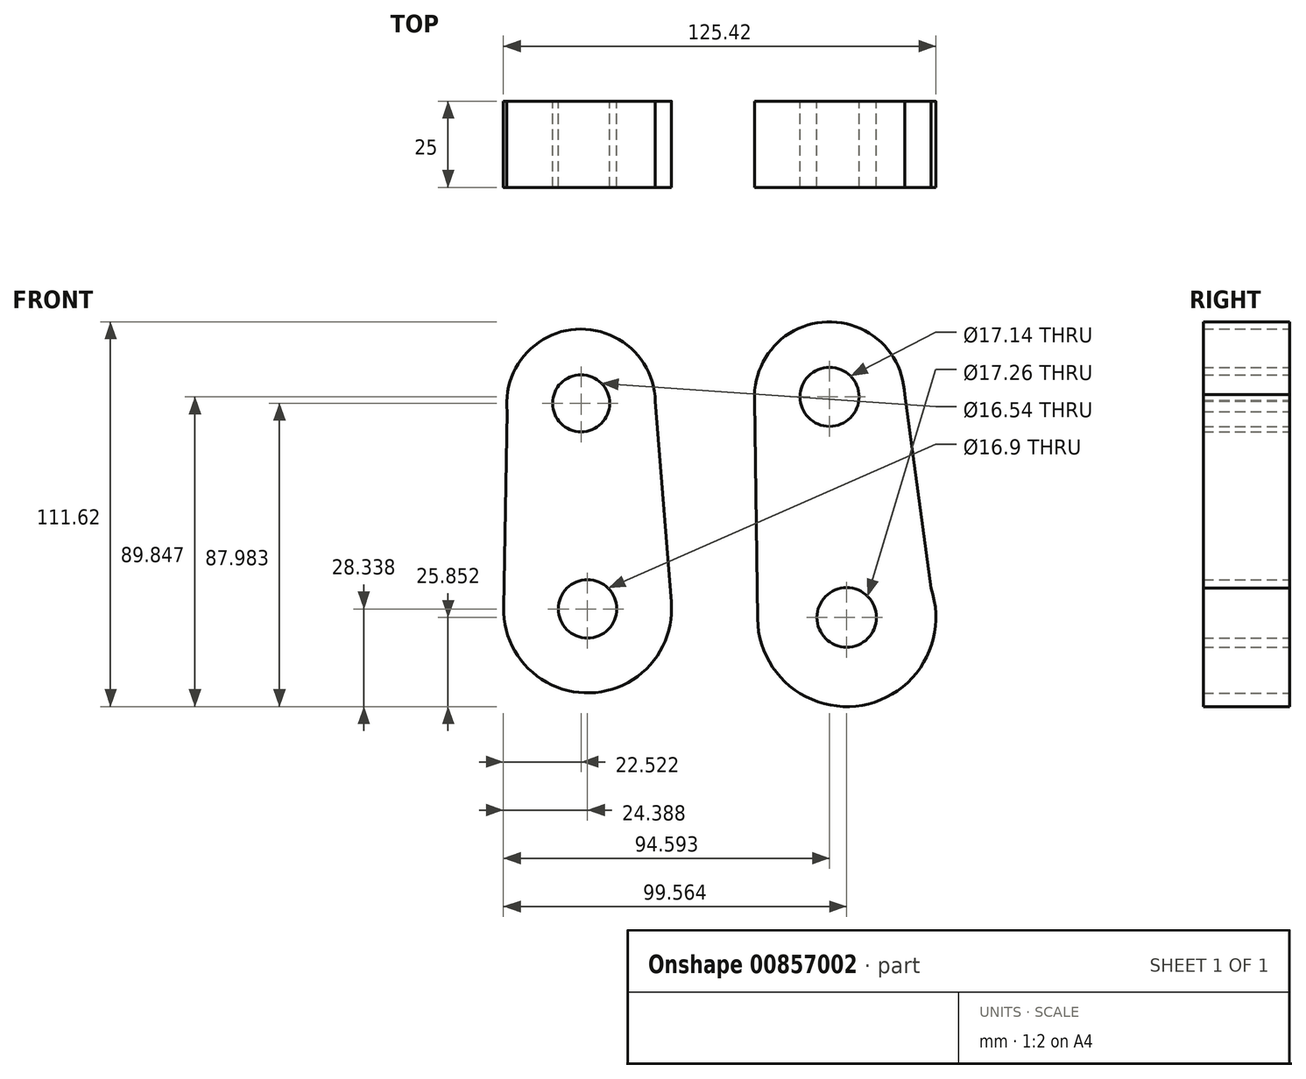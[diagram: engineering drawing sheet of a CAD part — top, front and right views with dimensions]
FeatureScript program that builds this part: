
annotation { "Feature Type Name" : "Feature", "Feature Type Description" : "" }
export const myFeature = defineFeature(function(context is Context, id is Id, definition is map)
    precondition{}
    {
        {
            var Q0;
            Q0=qCreatedBy(makeId("Front.planeOp"),FACE);
            var sketch = newSketch(context, id + "F0", { "sketchPlane" : qUnion([Q0])});
            skCircle(sketch, "E0", {"center": v(37.43, 27.03) * mm, "radius": 21.77 * mm});
            skCircle(sketch, "E1", {"center": v(-34.64, 25.16) * mm, "radius": 21.53 * mm});
            skCircle(sketch, "E2", {"center": v(-32.77, -34.48) * mm, "radius": 24.38 * mm});
            skCircle(sketch, "E3", {"center": v(42.4, -36.97) * mm, "radius": 25.86 * mm});
            skLineSegment(sketch, "E4", {"start": v(59.2, 27.63) * mm, "end": v(66.8, -28.43) * mm});
            skLineSegment(sketch, "E5", {"start": v(15.68, 26.1) * mm, "end": v(16.55, -37.32) * mm});
            skLineSegment(sketch, "E6", {"start": v(-13.11, 25.76) * mm, "end": v(-8.08, -37.32) * mm});
            skLineSegment(sketch, "E7", {"start": v(-56.03, 22.72) * mm, "end": v(-57.15, -34) * mm});
            skCircle(sketch, "E8", {"center": v(37.43, 27.03) * mm, "radius": 8.57 * mm});
            skCircle(sketch, "E9", {"center": v(-34.64, 25.16) * mm, "radius": 8.27 * mm});
            skCircle(sketch, "E10", {"center": v(42.4, -36.97) * mm, "radius": 8.63 * mm});
            skCircle(sketch, "E11", {"center": v(-32.77, -34.48) * mm, "radius": 8.45 * mm});
            skCircle(sketch, "E12.0", {"center": v(42.4, -36.97) * mm, "radius": 37.86 * mm, "construction": true});
            skSolve(sketch);
        }
        {
            var Q0;
            Q0 = qSketchRegion(id + "F0", true);
            extrude(context, id + "F1", {"entities" : qUnion([Q0]), "depth" : 25 * mm, "offsetDistance" : 25 * mm});
        }
    });
